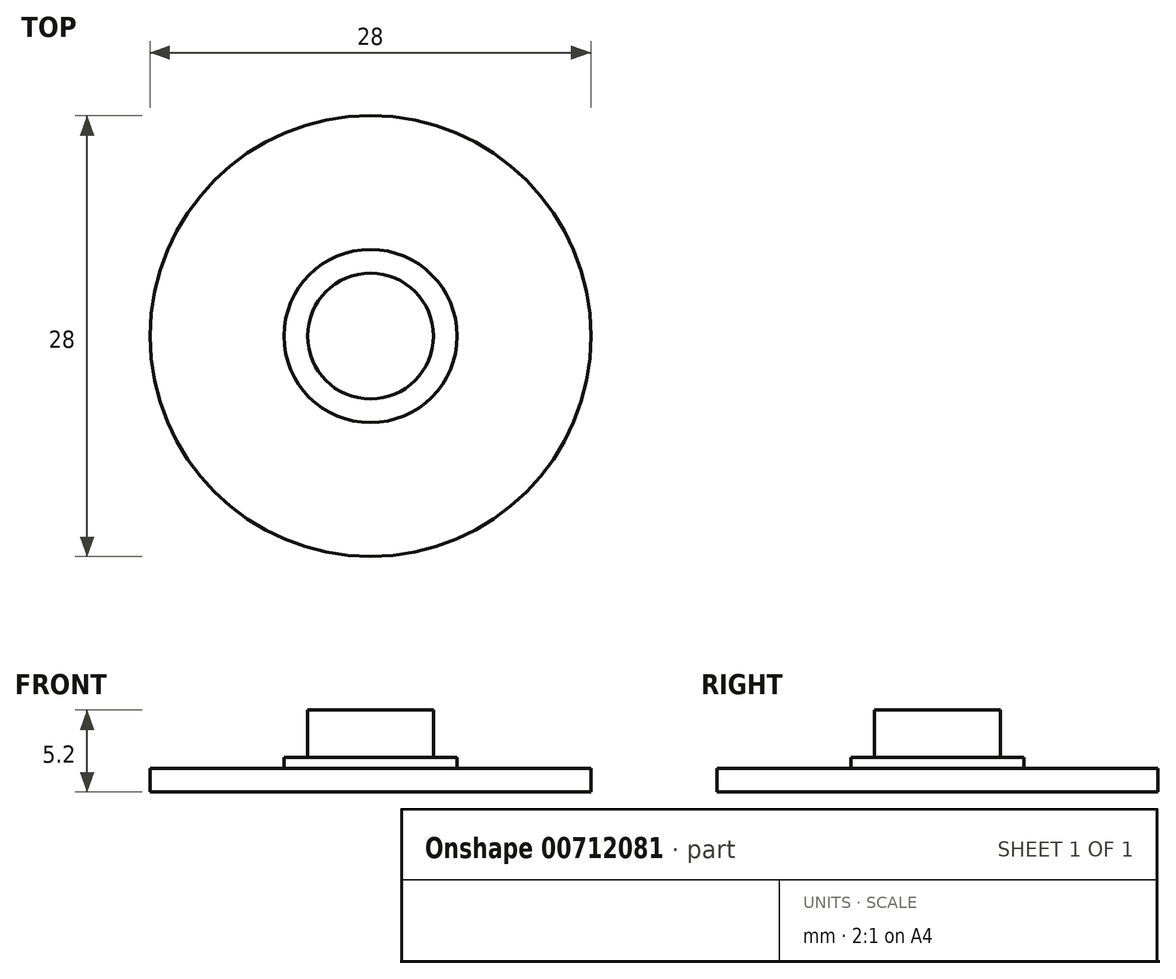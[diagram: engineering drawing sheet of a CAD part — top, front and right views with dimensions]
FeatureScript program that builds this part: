
annotation { "Feature Type Name" : "Feature", "Feature Type Description" : "" }
export const myFeature = defineFeature(function(context is Context, id is Id, definition is map)
    precondition{}
    {
        {
            var Q0;
            Q0=qCreatedBy(makeId("Top.planeOp"),FACE);
            var sketch = newSketch(context, id + "F0", { "sketchPlane" : qUnion([Q0])});
            skCircle(sketch, "E0", {"center": v(24.7, 0.21) * mm, "radius": 14 * mm});
            skCircle(sketch, "E1", {"center": v(24.7, 0.21) * mm, "radius": 5.5 * mm});
            skCircle(sketch, "E2", {"center": v(24.7, 0.21) * mm, "radius": 4 * mm});
            skSolve(sketch);
        }
        {
            var Q0;
            Q0=makeQuery(id+"F0.imprint","IMPRINT",FACE,{"disambiguationData":[TD([[makeQuery(id+"F0.imprint","IMPRINT",EDGE,{"derivedFrom":sQuery(id+"F0.wireOp",EDGE,"E0")}),1.0]])]});
            extrude(context, id + "F1", {"entities" : qUnion([Q0]), "depth" : 1.5 * mm, "offsetDistance" : 25 * mm});
        }
        {
            var Q0;
            Q0=makeQuery(id+"F0.imprint","IMPRINT",FACE,{"disambiguationData":[TD([[makeQuery(id+"F0.imprint","IMPRINT",EDGE,{"derivedFrom":sQuery(id+"F0.wireOp",EDGE,"E1")}),1.0]])]});
            extrude(context, id + "F2", {"entities" : qUnion([Q0]), "operationType" : NewBodyOperationType.ADD, "depth" : 2.2 * mm, "offsetDistance" : 25 * mm});
        }
        {
            var Q0;
            Q0=makeQuery(id+"F0.imprint","IMPRINT",FACE,{"disambiguationData":[TD([[makeQuery(id+"F0.imprint","IMPRINT",EDGE,{"derivedFrom":sQuery(id+"F0.wireOp",EDGE,"E2")}),1.0]])]});
            extrude(context, id + "F3", {"entities" : qUnion([Q0]), "operationType" : NewBodyOperationType.ADD, "depth" : 2.2 * mm, "offsetDistance" : 25 * mm});
        }
        {
            var Q0;
            {var subQ0=sQuery(id+"F0.wireOp",EDGE,"E2");Q0=makeQuery(id+"F3.boolean.opBoolean","MERGE",FACE,{"derivedFrom":[makeQuery(id+"F2.opExtrude","CAP_FACE",FACE,{"disambiguationData":[OSD([sQuery(id+"F0.wireOp",EDGE,"E1"),subQ0])],"isStart":false}),makeQuery(id+"F3.opExtrude","CAP_FACE",FACE,{"disambiguationData":[OSD([subQ0])],"isStart":false})]});}
            var sketch = newSketch(context, id + "F4", { "sketchPlane" : qUnion([Q0])});
            skCircle(sketch, "E3", {"center": v(24.7, 0.21) * mm, "radius": 4 * mm});
            skSolve(sketch);
        }
        {
            var Q0;
            Q0 = qSketchRegion(id + "F4", true);
            extrude(context, id + "F5", {"entities" : qUnion([Q0]), "operationType" : NewBodyOperationType.ADD, "depth" : 3 * mm, "offsetDistance" : 25 * mm});
        }
    });
